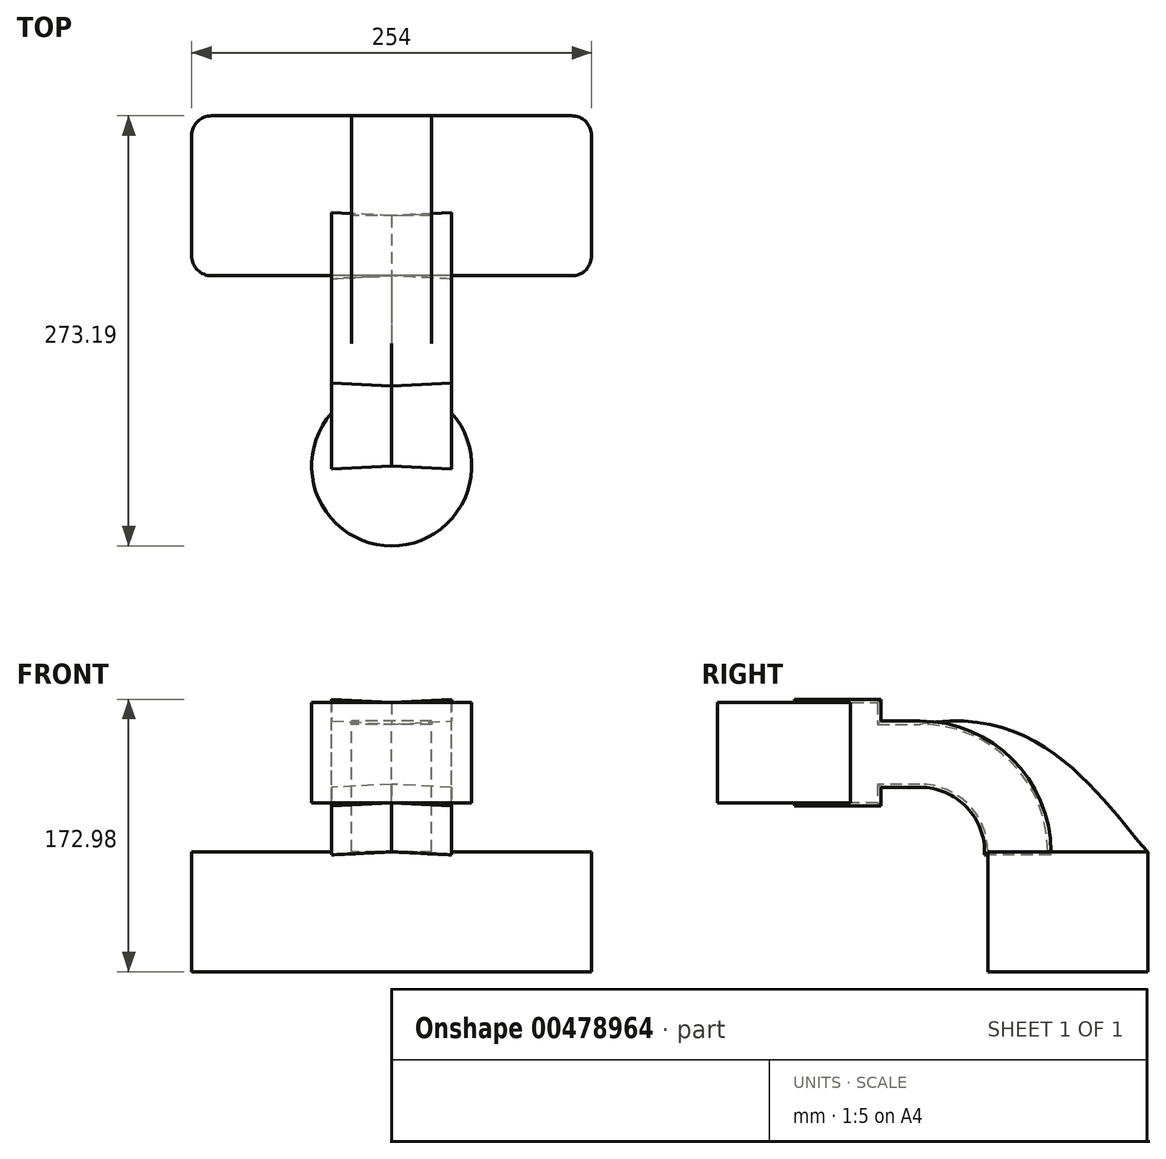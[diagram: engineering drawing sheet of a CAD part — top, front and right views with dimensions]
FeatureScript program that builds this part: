
annotation { "Feature Type Name" : "Feature", "Feature Type Description" : "" }
export const myFeature = defineFeature(function(context is Context, id is Id, definition is map)
    precondition{}
    {
        {
            var Q0;
            Q0=qCreatedBy(makeId("Right.planeOp"),FACE);
            var sketch = newSketch(context, id + "F0", { "sketchPlane" : qUnion([Q0])});
            skLineSegment(sketch, "E0.bottom", {"start": v(50.8, 38.1) * mm, "end": v(-50.8, 38.1) * mm});
            skLineSegment(sketch, "E0.top", {"start": v(50.8, -38.1) * mm, "end": v(-50.8, -38.1) * mm});
            skLineSegment(sketch, "E0.left", {"start": v(50.8, 38.1) * mm, "end": v(50.8, -38.1) * mm});
            skLineSegment(sketch, "E0.right", {"start": v(-50.8, 38.1) * mm, "end": v(-50.8, -38.1) * mm});
            skPoint(sketch, "E0.middle", {"position": v(0, 0) * mm});
            skLineSegment(sketch, "E1.bottom", {"start": v(-120.8, 132.89) * mm, "end": v(-222.4, 132.89) * mm});
            skLineSegment(sketch, "E1.top", {"start": v(-120.8, 69.19) * mm, "end": v(-222.4, 69.19) * mm});
            skLineSegment(sketch, "E1.left", {"start": v(-120.8, 132.89) * mm, "end": v(-120.8, 69.19) * mm});
            skLineSegment(sketch, "E1.right", {"start": v(-222.4, 132.89) * mm, "end": v(-222.4, 69.19) * mm});
            skPoint(sketch, "E1.middle", {"position": v(-171.6, 101.04) * mm});
            skArc(sketch, "E2", {"start": v(-50.8, 38.1) * mm, "mid": v(-63.37, 68.46) * mm, "end": v(-93.73, 81.03) * mm});
            skLineSegment(sketch, "E3", {"start": v(-93.73, 81.03) * mm, "end": v(-170.75, 81.03) * mm});
            skLineSegment(sketch, "E4.0", {"start": v(-93.73, 119.13) * mm, "end": v(-170.9, 119.13) * mm});
            skArc(sketch, "E4.1", {"start": v(-12.7, 38.1) * mm, "mid": v(-36.43, 95.4) * mm, "end": v(-93.73, 119.13) * mm});
            skFitSpline(sketch, "E5", {"points": [v(50.8, 38.1) * mm, v(-93.73, 119.13) * mm], "startDerivative": vector(-86.72, 94.62) * mm, "endDerivative": vector(-236.72, -43.83) * mm});
            skLineSegment(sketch, "E6", {"start": v(-171.6, 132.89) * mm, "end": v(-171.6, 69.19) * mm});
            skSolve(sketch);
        }
        {
            var Q0;
            Q0=makeQuery(id+"F0.imprint","IMPRINT",FACE,{"disambiguationData":[TD([[makeQuery(id+"F0.imprint","IMPRINT",EDGE,{"derivedFrom":sQuery(id+"F0.wireOp",EDGE,"E0.top")}),-1.0]])]});
            extrude(context, id + "F1", {"entities" : qUnion([Q0]), "depth" : 254 * mm, "symmetric" : true});
        }
        {
            var Q0;
            {var subQ1=sQuery(id+"F0.wireOp",EDGE,"E2");Q0=makeQuery(id+"F0.imprint","IMPRINT",FACE,{"disambiguationData":[TD([[makeQuery(id+"F0.imprint","IMPRINT",EDGE,{"derivedFrom":subQ1}),-1.0]])]});}
            var Q1;
            {var subQ6=sQuery(id+"F0.wireOp",EDGE,"E6");Q1=makeQuery(id+"F0.imprint","IMPRINT",FACE,{"disambiguationData":[TD([[makeQuery(id+"F0.imprint","IMPRINT",EDGE,{"derivedFrom":subQ6}),1.0]])]});}
            var Q2;
            Q2 = qConstructionFilter(qBodyType(qCreatedBy(id + "F0" ,EDGE), BodyType.WIRE), ConstructionObject.NO);
            extrude(context, id + "F2", {"entities" : qUnion([Q0, Q1]), "surfaceEntities" : qUnion([Q2]), "depth" : 76.2 * mm, "hasDraft" : true, "draftAngle" : 3 * degree, "symmetric" : true});
        }
        {
            var Q0;
            {var subQ2=sQuery(id+"F0.wireOp",EDGE,"E4.1");Q0=makeQuery(id+"F0.imprint","IMPRINT",FACE,{"disambiguationData":[TD([[makeQuery(id+"F0.imprint","IMPRINT",EDGE,{"derivedFrom":subQ2}),-1.0]])]});}
            extrude(context, id + "F3", {"entities" : qUnion([Q0]), "depth" : 50.8 * mm, "symmetric" : true});
        }
        {
            var Q0;
            {var subQ6=sQuery(id+"F0.wireOp",EDGE,"E6");Q0=makeQuery(id+"F0.imprint","IMPRINT",FACE,{"disambiguationData":[TD([[makeQuery(id+"F0.imprint","IMPRINT",EDGE,{"derivedFrom":subQ6}),1.0]])]});}
            var Q1;
            Q1=sQuery(id+"F0.wireOp",EDGE,"E6");
            revolve(context, id + "F4", {"operationType" : NewBodyOperationType.ADD, "entities" : qUnion([Q0]), "axis" : qUnion([Q1]), "revolveType" : RevolveType.FULL});
        }
        {
            var Q0;
            Q0=makeQuery(id+"F1.opExtrude","CAP_EDGE",EDGE,{"disambiguationData":[OSD([sQuery(id+"F0.wireOp",EDGE,"E0.left")])],"isStart":true});
            var Q1;
            Q1=makeQuery(id+"F1.opExtrude","CAP_EDGE",EDGE,{"disambiguationData":[OSD([sQuery(id+"F0.wireOp",EDGE,"E0.right")])],"isStart":true});
            var Q2;
            Q2=makeQuery(id+"F1.opExtrude","CAP_EDGE",EDGE,{"disambiguationData":[OSD([sQuery(id+"F0.wireOp",EDGE,"E0.right")])],"isStart":false});
            var Q3;
            Q3=makeQuery(id+"F1.opExtrude","CAP_EDGE",EDGE,{"disambiguationData":[OSD([sQuery(id+"F0.wireOp",EDGE,"E0.left")])],"isStart":false});
            fillet(context, id + "F5", {"entities" : qUnion([Q0, Q1, Q2, Q3]), "radius" : 12.7 * mm, "tangentPropagation" : true, "allowEdgeOverflow" : false});
        }
    });
